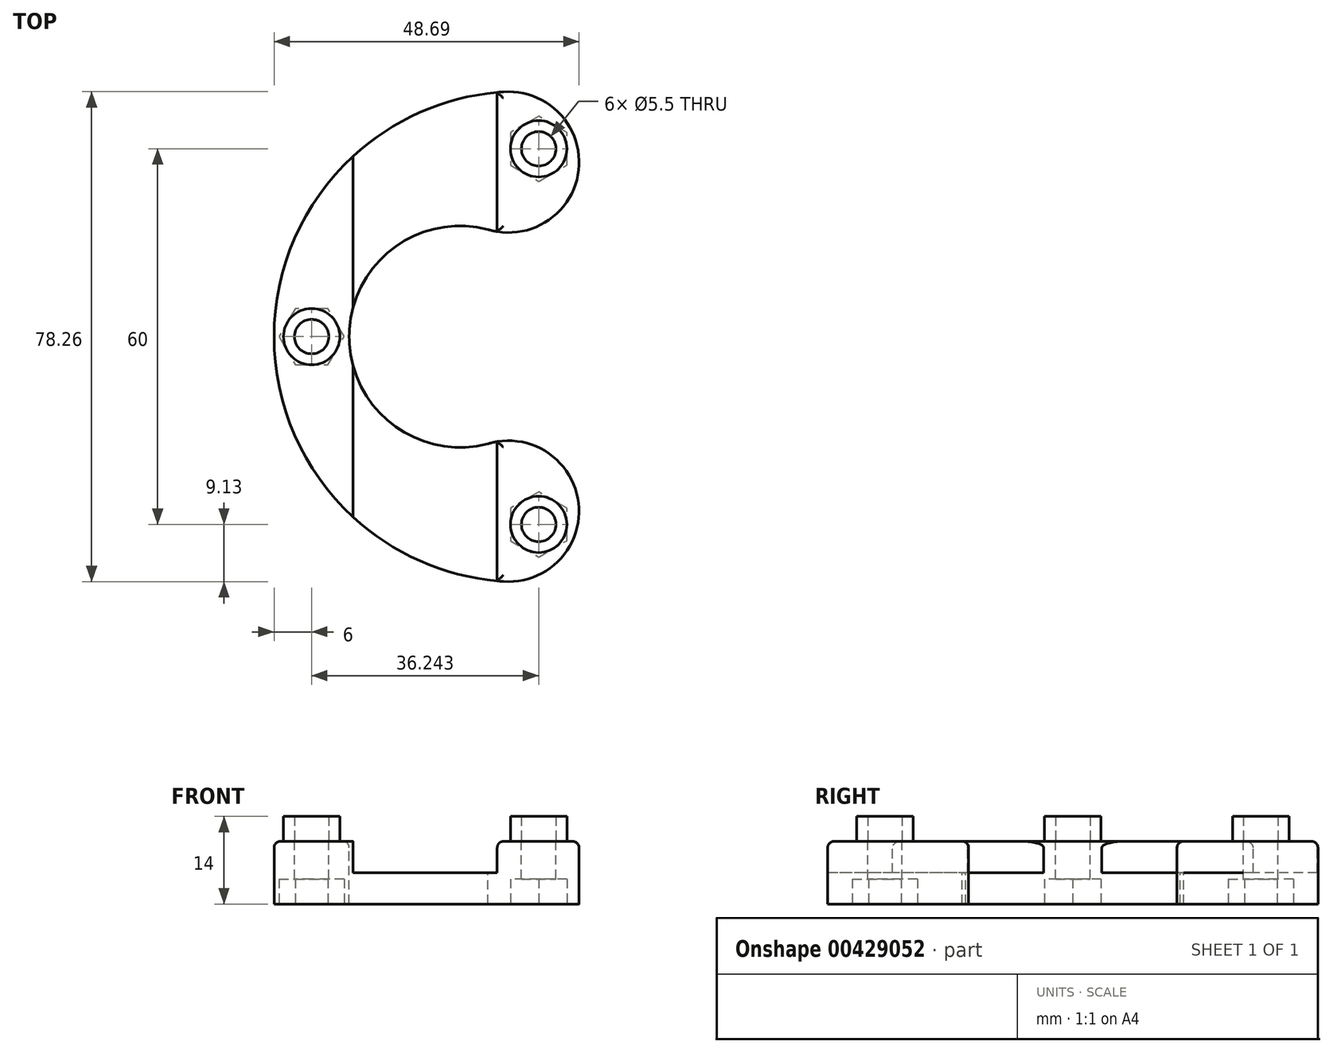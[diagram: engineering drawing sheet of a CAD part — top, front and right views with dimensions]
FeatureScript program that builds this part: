
annotation { "Feature Type Name" : "Feature", "Feature Type Description" : "" }
export const myFeature = defineFeature(function(context is Context, id is Id, definition is map)
    precondition{}
    {
        {
            var Q0;
            Q0=qCreatedBy(makeId("Top.planeOp"),FACE);
            var sketch = newSketch(context, id + "F0", { "sketchPlane" : qUnion([Q0])});
            skLineSegment(sketch, "E0", {"start": v(-10, 40) * mm, "end": v(-10, -40) * mm, "construction": true});
            skLineSegment(sketch, "E1.MirrorCS", {"start": v(10, 40) * mm, "end": v(10, -40) * mm, "construction": true});
            skPoint(sketch, "E2", {"position": v(18.12, 30) * mm});
            skPoint(sketch, "E3", {"position": v(-18.12, 0) * mm});
            skPoint(sketch, "E4", {"position": v(18.12, -30) * mm});
            skCircle(sketch, "E5", {"center": v(18.12, 30) * mm, "radius": 2.75 * mm});
            skCircle(sketch, "E6", {"center": v(-18.12, 0) * mm, "radius": 2.75 * mm});
            skCircle(sketch, "E7", {"center": v(18.12, -30) * mm, "radius": 2.75 * mm});
            skCircle(sketch, "E8", {"center": v(18.12, 30) * mm, "radius": 10.7 * mm, "construction": true});
            skCircle(sketch, "E9", {"center": v(-18.12, 0) * mm, "radius": 10.7 * mm, "construction": true});
            skCircle(sketch, "E10", {"center": v(18.12, -30) * mm, "radius": 10.7 * mm, "construction": true});
            skPoint(sketch, "E11", {"position": v(-14, 14.11) * mm});
            skPoint(sketch, "E12.MirrorP", {"position": v(-14, -14.11) * mm});
            skPoint(sketch, "E13", {"position": v(14, 15.89) * mm});
            skArc(sketch, "E14", {"start": v(12.49, 39.1) * mm, "mid": v(-24.12, 0) * mm, "end": v(12.5, -39.1) * mm});
            skArc(sketch, "E15", {"start": v(10, 17.12) * mm, "mid": v(-12.12, 0) * mm, "end": v(10, -17.12) * mm});
            skArc(sketch, "E16", {"start": v(10, 17.12) * mm, "mid": v(24.5, 26.6) * mm, "end": v(12.49, 39.1) * mm});
            skArc(sketch, "E17", {"start": v(12.5, -39.1) * mm, "mid": v(24.48, -26.6) * mm, "end": v(10, -17.12) * mm});
            skSolve(sketch);
        }
        {
            var Q0;
            Q0 = qSketchRegion(id + "F0", true);
            extrude(context, id + "F1", {"entities" : qUnion([Q0]), "oppositeDirection" : true, "offsetDistance" : 25 * mm, "depth" : 10 * mm});
        }
        {
            var Q0;
            Q0=makeQuery(id+"F1.opExtrude","CAP_FACE",FACE,{"disambiguationData":[OSD([sQuery(id+"F0.wireOp",EDGE,"E5"),sQuery(id+"F0.wireOp",EDGE,"E6"),sQuery(id+"F0.wireOp",EDGE,"E7"),sQuery(id+"F0.wireOp",EDGE,"E14"),sQuery(id+"F0.wireOp",EDGE,"E15"),sQuery(id+"F0.wireOp",EDGE,"E16"),sQuery(id+"F0.wireOp",EDGE,"E17")])],"isStart":true});
            var sketch = newSketch(context, id + "F2", { "sketchPlane" : qUnion([Q0])});
            skLineSegment(sketch, "E18", {"start": v(-11.5, 32.23) * mm, "end": v(-11.5, -30.71) * mm});
            skLineSegment(sketch, "E19", {"start": v(11.5, 41.58) * mm, "end": v(11.5, -41.14) * mm});
            skArc(sketch, "E20", {"start": v(11.5, 41.58) * mm, "mid": v(-0.74, 38.74) * mm, "end": v(-11.5, 32.23) * mm});
            skArc(sketch, "E21", {"start": v(-11.5, -30.71) * mm, "mid": v(-0.84, -37.79) * mm, "end": v(11.5, -41.14) * mm});
            skSolve(sketch);
        }
        {
            var Q0;
            Q0 = qSketchRegion(id + "F2", true);
            extrude(context, id + "F3", {"entities" : qUnion([Q0]), "operationType" : NewBodyOperationType.REMOVE, "oppositeDirection" : true, "offsetDistance" : 25 * mm, "depth" : 5 * mm});
        }
        {
            var Q0;
            Q0=makeQuery(id+"F3.boolean.opBoolean","COPY",EDGE,{"disambiguationData":[OD(1.0)],"derivedFrom":makeQuery(id+"F3.opExtrude","CAP_EDGE",EDGE,{"disambiguationData":[OSD([sQuery(id+"F2.wireOp",EDGE,"E18")])],"isStart":true})});
            var Q1;
            Q1=makeQuery(id+"F3.boolean.opBoolean","COPY",EDGE,{"disambiguationData":[OD(0.0)],"derivedFrom":makeQuery(id+"F3.opExtrude","CAP_EDGE",EDGE,{"disambiguationData":[OSD([sQuery(id+"F2.wireOp",EDGE,"E18")])],"isStart":true})});
            var Q2;
            Q2=makeQuery(id+"F1.opExtrude","CAP_EDGE",EDGE,{"disambiguationData":[OSD([sQuery(id+"F0.wireOp",EDGE,"E15")])],"isStart":true});
            var Q3;
            {var subQ0=sQuery(id+"F0.wireOp",EDGE,"E17");var subQ2=sQuery(id+"F2.wireOp",EDGE,"E19");Q3=makeQuery(id+"F3.boolean.opBoolean","COPY",EDGE,{"disambiguationData":[TD([makeQuery(id+"F1.opExtrude","SWEPT_FACE",FACE,{"disambiguationData":[OSD([subQ0])]})])],"derivedFrom":makeQuery(id+"F3.opExtrude","CAP_EDGE",EDGE,{"disambiguationData":[OSD([subQ2])],"isStart":true})});}
            var Q4;
            {var subQ0=sQuery(id+"F0.wireOp",EDGE,"E16");var subQ2=sQuery(id+"F2.wireOp",EDGE,"E19");Q4=makeQuery(id+"F3.boolean.opBoolean","COPY",EDGE,{"disambiguationData":[TD([makeQuery(id+"F1.opExtrude","SWEPT_FACE",FACE,{"disambiguationData":[OSD([subQ0])]})])],"derivedFrom":makeQuery(id+"F3.opExtrude","CAP_EDGE",EDGE,{"disambiguationData":[OSD([subQ2])],"isStart":true})});}
            var Q5;
            {var subQ0=sQuery(id+"F0.wireOp",EDGE,"E14");Q5=makeQuery(id+"F3.boolean.opBoolean","SPLIT",EDGE,{"disambiguationData":[TD([makeQuery(id+"F3.opExtrude","SWEPT_FACE",FACE,{"disambiguationData":[OSD([sQuery(id+"F2.wireOp",EDGE,"E18")])]})])],"derivedFrom":makeQuery(id+"F1.opExtrude","CAP_EDGE",EDGE,{"disambiguationData":[OSD([subQ0])],"isStart":true})});}
            var Q6;
            Q6=makeQuery(id+"F1.opExtrude","CAP_EDGE",EDGE,{"disambiguationData":[OSD([sQuery(id+"F0.wireOp",EDGE,"E16")])],"isStart":true});
            var Q7;
            Q7=makeQuery(id+"F1.opExtrude","CAP_EDGE",EDGE,{"disambiguationData":[OSD([sQuery(id+"F0.wireOp",EDGE,"E17")])],"isStart":true});
            fillet(context, id + "F4", {"entities" : qUnion([Q0, Q1, Q2, Q3, Q4, Q5, Q6, Q7]), "radius" : 1 * mm, "tangentPropagation" : true, "allowEdgeOverflow" : false});
        }
        {
            var Q0;
            Q0=makeQuery(id+"F1.opExtrude","CAP_FACE",FACE,{"disambiguationData":[OSD([sQuery(id+"F0.wireOp",EDGE,"E5"),sQuery(id+"F0.wireOp",EDGE,"E6"),sQuery(id+"F0.wireOp",EDGE,"E7"),sQuery(id+"F0.wireOp",EDGE,"E14"),sQuery(id+"F0.wireOp",EDGE,"E15"),sQuery(id+"F0.wireOp",EDGE,"E16"),sQuery(id+"F0.wireOp",EDGE,"E17")])],"isStart":false});
            var sketch = newSketch(context, id + "F5", { "sketchPlane" : qUnion([Q0])});
            skCircle(sketch, "E22.cCircle", {"center": v(18.12, 30) * mm, "radius": 4.5 * mm, "construction": true});
            skLineSegment(sketch, "E22.0", {"start": v(13.62, 27.4) * mm, "end": v(13.62, 32.6) * mm});
            skLineSegment(sketch, "E22.1", {"start": v(13.62, 32.6) * mm, "end": v(18.12, 35.2) * mm});
            skLineSegment(sketch, "E22.2", {"start": v(18.12, 35.2) * mm, "end": v(22.62, 32.6) * mm});
            skLineSegment(sketch, "E22.3", {"start": v(22.62, 32.6) * mm, "end": v(22.62, 27.4) * mm});
            skLineSegment(sketch, "E22.4", {"start": v(22.62, 27.4) * mm, "end": v(18.12, 24.8) * mm});
            skLineSegment(sketch, "E22.5", {"start": v(18.12, 24.8) * mm, "end": v(13.62, 27.4) * mm});
            skPoint(sketch, "E22.0.midPoint", {"position": v(13.62, 30) * mm});
            skCircle(sketch, "E23.cCircle", {"center": v(-18.12, 0) * mm, "radius": 4.5 * mm, "construction": true});
            skLineSegment(sketch, "E23.0", {"start": v(-20.72, 4.5) * mm, "end": v(-15.52, 4.5) * mm});
            skLineSegment(sketch, "E23.1", {"start": v(-15.52, 4.5) * mm, "end": v(-12.92, 0) * mm});
            skLineSegment(sketch, "E23.2", {"start": v(-12.92, 0) * mm, "end": v(-15.52, -4.5) * mm});
            skLineSegment(sketch, "E23.3", {"start": v(-15.52, -4.5) * mm, "end": v(-20.72, -4.5) * mm});
            skLineSegment(sketch, "E23.4", {"start": v(-20.72, -4.5) * mm, "end": v(-23.32, 0) * mm});
            skLineSegment(sketch, "E23.5", {"start": v(-23.32, 0) * mm, "end": v(-20.72, 4.5) * mm});
            skPoint(sketch, "E23.0.midPoint", {"position": v(-18.12, 4.5) * mm});
            skCircle(sketch, "E24.cCircle", {"center": v(18.12, -30) * mm, "radius": 4.5 * mm, "construction": true});
            skLineSegment(sketch, "E24.0", {"start": v(22.62, -27.4) * mm, "end": v(22.62, -32.6) * mm});
            skLineSegment(sketch, "E24.1", {"start": v(22.62, -32.6) * mm, "end": v(18.12, -35.2) * mm});
            skLineSegment(sketch, "E24.2", {"start": v(18.12, -35.2) * mm, "end": v(13.62, -32.6) * mm});
            skLineSegment(sketch, "E24.3", {"start": v(13.62, -32.6) * mm, "end": v(13.62, -27.4) * mm});
            skLineSegment(sketch, "E24.4", {"start": v(13.62, -27.4) * mm, "end": v(18.12, -24.8) * mm});
            skLineSegment(sketch, "E24.5", {"start": v(18.12, -24.8) * mm, "end": v(22.62, -27.4) * mm});
            skPoint(sketch, "E24.0.midPoint", {"position": v(22.62, -30) * mm});
            skSolve(sketch);
        }
        {
            var Q0;
            Q0 = qSketchRegion(id + "F5", true);
            extrude(context, id + "F6", {"entities" : qUnion([Q0]), "operationType" : NewBodyOperationType.REMOVE, "oppositeDirection" : true, "offsetDistance" : 25 * mm, "depth" : 4 * mm});
        }
        {
            var Q0;
            Q0=makeQuery(id+"F0.imprint","IMPRINT",FACE,{"disambiguationData":[TD([[makeQuery(id+"F0.imprint","IMPRINT",EDGE,{"derivedFrom":sQuery(id+"F0.wireOp",EDGE,"E5")}),-1.0]])]});
            var sketch = newSketch(context, id + "F7", { "sketchPlane" : qUnion([Q0])});
            skCircle(sketch, "E25", {"center": v(18.12, 30) * mm, "radius": 2.75 * mm});
            skCircle(sketch, "E26", {"center": v(-18.12, 0) * mm, "radius": 2.75 * mm});
            skCircle(sketch, "E27", {"center": v(18.12, -30) * mm, "radius": 2.75 * mm});
            skCircle(sketch, "E28", {"center": v(-18.12, 0) * mm, "radius": 4.5 * mm});
            skCircle(sketch, "E29", {"center": v(18.12, -30) * mm, "radius": 4.5 * mm});
            skCircle(sketch, "E30", {"center": v(18.12, 30) * mm, "radius": 4.5 * mm});
            skSolve(sketch);
        }
        {
            var Q0;
            Q0 = qSketchRegion(id + "F7", true);
            extrude(context, id + "F8", {"entities" : qUnion([Q0]), "operationType" : NewBodyOperationType.ADD, "offsetDistance" : 25 * mm, "depth" : 4 * mm});
        }
    });
